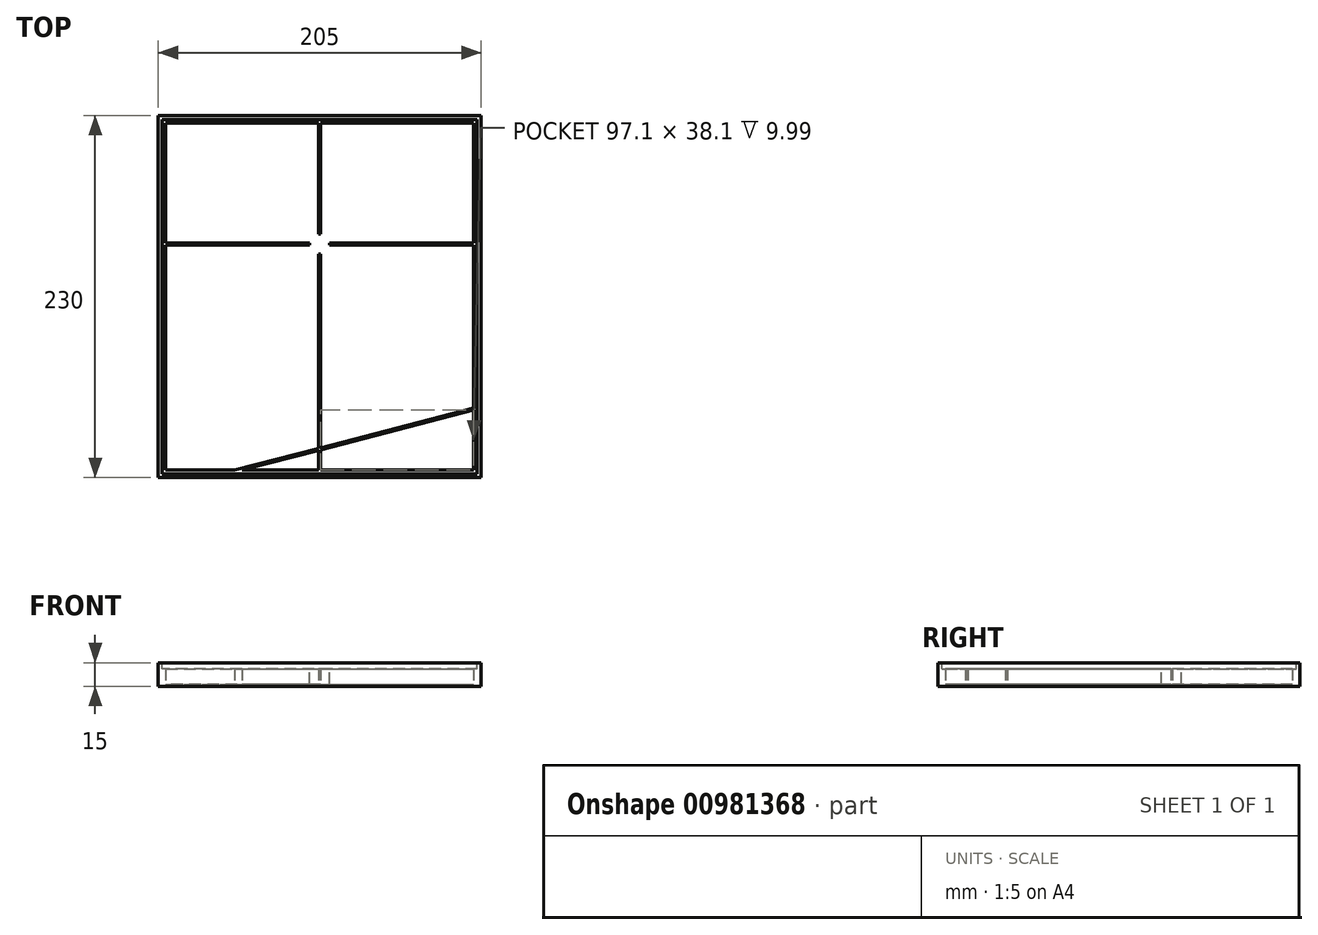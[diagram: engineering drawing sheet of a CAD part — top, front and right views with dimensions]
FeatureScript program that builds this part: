
annotation { "Feature Type Name" : "Feature", "Feature Type Description" : "" }
export const myFeature = defineFeature(function(context is Context, id is Id, definition is map)
    precondition{}
    {
        {
            var Q0;
            Q0=qCreatedBy(makeId("Top.planeOp"),FACE);
            var sketch = newSketch(context, id + "F0", { "sketchPlane" : qUnion([Q0])});
            skLineSegment(sketch, "E0.bottom", {"start": v(0, 0) * mm, "end": v(205, 0) * mm});
            skLineSegment(sketch, "E0.top", {"start": v(0, 230) * mm, "end": v(205, 230) * mm});
            skLineSegment(sketch, "E0.left", {"start": v(0, 0) * mm, "end": v(0, 230) * mm});
            skLineSegment(sketch, "E0.right", {"start": v(205, 0) * mm, "end": v(205, 230) * mm});
            skSolve(sketch);
        }
        {
            var Q0;
            Q0=makeQuery(id+"F0.imprint","IMPRINT",FACE,{"disambiguationData":[TD([[makeQuery(id+"F0.imprint","IMPRINT",EDGE,{"derivedFrom":sQuery(id+"F0.wireOp",EDGE,"E0.bottom")}),1.0]])]});
            extrude(context, id + "F1", {"entities" : qUnion([Q0]), "depth" : 15 * mm, "offsetDistance" : 25 * mm});
        }
        {
            var Q0;
            Q0=makeQuery(id+"F1.opExtrude","CAP_FACE",FACE,{"disambiguationData":[OSD([sQuery(id+"F0.wireOp",EDGE,"E0.bottom"),sQuery(id+"F0.wireOp",EDGE,"E0.top"),sQuery(id+"F0.wireOp",EDGE,"E0.left"),sQuery(id+"F0.wireOp",EDGE,"E0.right")])],"isStart":false});
            var sketch = newSketch(context, id + "F2", { "sketchPlane" : qUnion([Q0])});
            skLineSegment(sketch, "E1.bottom", {"start": v(2.4, 227.6) * mm, "end": v(202.6, 227.6) * mm});
            skLineSegment(sketch, "E1.top", {"start": v(2.4, 2.4) * mm, "end": v(202.6, 2.4) * mm});
            skLineSegment(sketch, "E1.left", {"start": v(2.4, 227.6) * mm, "end": v(2.4, 2.4) * mm});
            skLineSegment(sketch, "E1.right", {"start": v(202.6, 227.6) * mm, "end": v(202.6, 2.4) * mm});
            skSolve(sketch);
        }
        {
            var Q0;
            Q0=makeQuery(id+"F2.imprint","IMPRINT",FACE,{"disambiguationData":[TD([[makeQuery(id+"F2.imprint","IMPRINT",EDGE,{"derivedFrom":sQuery(id+"F2.wireOp",EDGE,"E1.bottom")}),-1.0]])]});
            extrude(context, id + "F3", {"entities" : qUnion([Q0]), "operationType" : NewBodyOperationType.REMOVE, "endBound" : BoundingType.UP_TO_NEXT, "oppositeDirection" : true, "depth" : 25 * mm, "hasOffset" : true, "offsetDistance" : 1.2 * mm});
        }
        {
            var Q0;
            Q0=makeQuery(id+"F3.boolean.opBoolean","COPY",FACE,{"derivedFrom":makeQuery(id+"F3.opExtrude","CAP_FACE",FACE,{"disambiguationData":[OSD([sQuery(id+"F2.wireOp",EDGE,"E1.bottom"),sQuery(id+"F2.wireOp",EDGE,"E1.top"),sQuery(id+"F2.wireOp",EDGE,"E1.left"),sQuery(id+"F2.wireOp",EDGE,"E1.right")])],"isStart":false})});
            var sketch = newSketch(context, id + "F4", { "sketchPlane" : qUnion([Q0])});
            skLineSegment(sketch, "E2.bottom", {"start": v(4.8, 225.2) * mm, "end": v(200.2, 225.2) * mm});
            skLineSegment(sketch, "E2.top", {"start": v(4.8, 4.8) * mm, "end": v(200.2, 4.8) * mm});
            skLineSegment(sketch, "E2.left", {"start": v(4.8, 225.2) * mm, "end": v(4.8, 4.8) * mm});
            skLineSegment(sketch, "E2.right", {"start": v(200.2, 225.2) * mm, "end": v(200.2, 4.8) * mm});
            skLineSegment(sketch, "E3", {"start": v(101.9, 225.2) * mm, "end": v(101.9, 149) * mm});
            skLineSegment(sketch, "E4", {"start": v(101.9, 149) * mm, "end": v(4.8, 149) * mm});
            skLineSegment(sketch, "E5", {"start": v(4.8, 149) * mm, "end": v(4.8, 147.8) * mm});
            skLineSegment(sketch, "E6", {"start": v(4.8, 147.8) * mm, "end": v(101.9, 147.8) * mm});
            skLineSegment(sketch, "E7", {"start": v(101.9, 147.8) * mm, "end": v(101.9, 4.8) * mm});
            skLineSegment(sketch, "E8", {"start": v(101.9, 4.8) * mm, "end": v(103.1, 4.8) * mm});
            skLineSegment(sketch, "E9", {"start": v(103.1, 4.8) * mm, "end": v(103.1, 147.8) * mm});
            skLineSegment(sketch, "E10", {"start": v(103.1, 147.8) * mm, "end": v(200.2, 147.8) * mm});
            skLineSegment(sketch, "E11", {"start": v(200.2, 147.8) * mm, "end": v(200.2, 149) * mm});
            skLineSegment(sketch, "E12", {"start": v(200.2, 149) * mm, "end": v(103.1, 149) * mm});
            skLineSegment(sketch, "E13", {"start": v(103.1, 149) * mm, "end": v(103.1, 225.2) * mm});
            skLineSegment(sketch, "E14", {"start": v(103.1, 225.2) * mm, "end": v(101.9, 225.2) * mm});
            skSolve(sketch);
        }
        {
            var Q0;
            Q0=makeQuery(id+"F4.imprint","IMPRINT",FACE,{"disambiguationData":[TD([[makeQuery(id+"F4.imprint","IMPRINT",EDGE,{"derivedFrom":sQuery(id+"F4.wireOp",EDGE,"E2.bottom")}),1.0]])]});
            var Q1;
            Q1=makeQuery(id+"F4.imprint","IMPRINT",FACE,{"disambiguationData":[TD([[makeQuery(id+"F4.imprint","IMPRINT",EDGE,{"derivedFrom":sQuery(id+"F4.wireOp",EDGE,"E3")}),1.0]])]});
            var Q2;
            Q2=makeQuery(id+"F1.opExtrude","CAP_FACE",FACE,{"disambiguationData":[OSD([sQuery(id+"F0.wireOp",EDGE,"E0.bottom"),sQuery(id+"F0.wireOp",EDGE,"E0.top"),sQuery(id+"F0.wireOp",EDGE,"E0.left"),sQuery(id+"F0.wireOp",EDGE,"E0.right")])],"isStart":false});
            extrude(context, id + "F5", {"entities" : qUnion([Q0, Q1]), "operationType" : NewBodyOperationType.ADD, "endBound" : BoundingType.UP_TO_SURFACE, "depth" : 19.05 * mm, "endBoundEntityFace" : qUnion([Q2]), "hasOffset" : true, "offsetDistance" : 3.8 * mm});
        }
        {
            var Q0;
            Q0=makeQuery(id+"F5.opExtrude","CAP_FACE",FACE,{"disambiguationData":[OSD([sQuery(id+"F2.wireOp",EDGE,"E1.bottom"),sQuery(id+"F2.wireOp",EDGE,"E1.top"),sQuery(id+"F2.wireOp",EDGE,"E1.left"),sQuery(id+"F2.wireOp",EDGE,"E1.right"),sQuery(id+"F4.wireOp",EDGE,"E2.bottom"),sQuery(id+"F4.wireOp",EDGE,"E2.top"),sQuery(id+"F4.wireOp",EDGE,"E2.left"),sQuery(id+"F4.wireOp",EDGE,"E2.right"),sQuery(id+"F4.wireOp",EDGE,"E3"),sQuery(id+"F4.wireOp",EDGE,"E4"),sQuery(id+"F4.wireOp",EDGE,"E6"),sQuery(id+"F4.wireOp",EDGE,"E7"),sQuery(id+"F4.wireOp",EDGE,"E9"),sQuery(id+"F4.wireOp",EDGE,"E10"),sQuery(id+"F4.wireOp",EDGE,"E12"),sQuery(id+"F4.wireOp",EDGE,"E13")])],"isStart":false});
            var sketch = newSketch(context, id + "F6", { "sketchPlane" : qUnion([Q0])});
            skLineSegment(sketch, "E15", {"start": v(103.1, 149) * mm, "end": v(101.9, 147.8) * mm});
            skLineSegment(sketch, "E16", {"start": v(101.9, 147.8) * mm, "end": v(101.9, 149) * mm});
            skLineSegment(sketch, "E17", {"start": v(101.9, 149) * mm, "end": v(103.1, 147.8) * mm});
            skCircle(sketch, "E18", {"center": v(102.5, 148.4) * mm, "radius": 6.35 * mm});
            skSolve(sketch);
        }
        {
            var Q0;
            {var subQ0=sQuery(id+"F6.wireOp",EDGE,"E18");var subQ1=makeQuery(id+"F5.opExtrude","CAP_EDGE",EDGE,{"disambiguationData":[OSD([sQuery(id+"F4.wireOp",EDGE,"E13")])],"isStart":false});var subQ2=makeQuery(id+"F6.imprint","INTERSECT",VERTEX,{"derivedFrom":[subQ1,subQ0]});Q0=makeQuery(id+"F6.imprint","IMPRINT",FACE,{"disambiguationData":[TD([[makeQuery(id+"F6.imprint","IMPRINT",EDGE,{"disambiguationData":[TD([[subQ2,1.0]])],"derivedFrom":subQ0}),1.0]])]});}
            var Q1;
            {var subQ3=sQuery(id+"F6.wireOp",EDGE,"E18");var subQ5=makeQuery(id+"F5.opExtrude","CAP_EDGE",EDGE,{"disambiguationData":[OSD([sQuery(id+"F4.wireOp",EDGE,"E13")])],"isStart":false});var subQ6=makeQuery(id+"F6.imprint","INTERSECT",VERTEX,{"derivedFrom":[subQ5,subQ3]});Q1=makeQuery(id+"F6.imprint","IMPRINT",FACE,{"disambiguationData":[TD([[makeQuery(id+"F6.imprint","IMPRINT",EDGE,{"disambiguationData":[TD([[subQ6,-1.0]])],"derivedFrom":subQ3}),1.0]])]});}
            var Q2;
            {var subQ0=sQuery(id+"F6.wireOp",EDGE,"E18");var subQ1=makeQuery(id+"F5.opExtrude","CAP_EDGE",EDGE,{"disambiguationData":[OSD([sQuery(id+"F4.wireOp",EDGE,"E3")])],"isStart":false});var subQ2=makeQuery(id+"F6.imprint","INTERSECT",VERTEX,{"derivedFrom":[subQ1,subQ0]});Q2=makeQuery(id+"F6.imprint","IMPRINT",FACE,{"disambiguationData":[TD([[makeQuery(id+"F6.imprint","IMPRINT",EDGE,{"disambiguationData":[TD([[subQ2,-1.0]])],"derivedFrom":subQ0}),1.0]])]});}
            var Q3;
            {var subQ0=sQuery(id+"F6.wireOp",EDGE,"E16");Q3=makeQuery(id+"F6.imprint","IMPRINT",FACE,{"disambiguationData":[TD([[makeQuery(id+"F6.imprint","IMPRINT",EDGE,{"derivedFrom":subQ0}),1.0]])]});}
            var Q4;
            {var subQ0=sQuery(id+"F6.wireOp",EDGE,"E16");Q4=makeQuery(id+"F6.imprint","IMPRINT",FACE,{"disambiguationData":[TD([[makeQuery(id+"F6.imprint","IMPRINT",EDGE,{"derivedFrom":subQ0}),-1.0]])]});}
            var Q5;
            {var subQ3=sQuery(id+"F6.wireOp",EDGE,"E18");var subQ5=makeQuery(id+"F5.opExtrude","CAP_EDGE",EDGE,{"disambiguationData":[OSD([sQuery(id+"F4.wireOp",EDGE,"E12")])],"isStart":false});var subQ6=makeQuery(id+"F6.imprint","INTERSECT",VERTEX,{"derivedFrom":[subQ5,subQ3]});Q5=makeQuery(id+"F6.imprint","IMPRINT",FACE,{"disambiguationData":[TD([[makeQuery(id+"F6.imprint","IMPRINT",EDGE,{"disambiguationData":[TD([[subQ6,1.0]])],"derivedFrom":subQ3}),1.0]])]});}
            var Q6;
            {var subQ1=makeQuery(id+"F5.opExtrude","CAP_EDGE",EDGE,{"disambiguationData":[OSD([sQuery(id+"F4.wireOp",EDGE,"E7")])],"isStart":false});var subQ3=sQuery(id+"F6.wireOp",EDGE,"E18");var subQ4=makeQuery(id+"F6.imprint","INTERSECT",VERTEX,{"derivedFrom":[subQ1,subQ3]});Q6=makeQuery(id+"F6.imprint","IMPRINT",FACE,{"disambiguationData":[TD([[makeQuery(id+"F6.imprint","IMPRINT",EDGE,{"disambiguationData":[TD([[subQ4,-1.0]])],"derivedFrom":subQ3}),1.0]])]});}
            var Q7;
            {var subQ0=sQuery(id+"F6.wireOp",EDGE,"E18");var subQ1=makeQuery(id+"F5.opExtrude","CAP_EDGE",EDGE,{"disambiguationData":[OSD([sQuery(id+"F4.wireOp",EDGE,"E9")])],"isStart":false});var subQ2=makeQuery(id+"F6.imprint","INTERSECT",VERTEX,{"derivedFrom":[subQ1,subQ0]});Q7=makeQuery(id+"F6.imprint","IMPRINT",FACE,{"disambiguationData":[TD([[makeQuery(id+"F6.imprint","IMPRINT",EDGE,{"disambiguationData":[TD([[subQ2,-1.0]])],"derivedFrom":subQ0}),1.0]])]});}
            var Q8;
            {var subQ0=sQuery(id+"F6.wireOp",EDGE,"E18");var subQ1=makeQuery(id+"F5.opExtrude","CAP_EDGE",EDGE,{"disambiguationData":[OSD([sQuery(id+"F4.wireOp",EDGE,"E6")])],"isStart":false});var subQ2=makeQuery(id+"F6.imprint","INTERSECT",VERTEX,{"derivedFrom":[subQ1,subQ0]});Q8=makeQuery(id+"F6.imprint","IMPRINT",FACE,{"disambiguationData":[TD([[makeQuery(id+"F6.imprint","IMPRINT",EDGE,{"disambiguationData":[TD([[subQ2,-1.0]])],"derivedFrom":subQ0}),1.0]])]});}
            var Q9;
            {var subQ4=sQuery(id+"F4.wireOp",EDGE,"E12");Q9=makeQuery(id+"F5.boolean.opBoolean","SPLIT",FACE,{"disambiguationData":[TD([makeQuery(id+"F5.opExtrude","SWEPT_FACE",FACE,{"disambiguationData":[OSD([subQ4])]})])],"derivedFrom":makeQuery(id+"F3.boolean.opBoolean","COPY",FACE,{"derivedFrom":makeQuery(id+"F3.opExtrude","CAP_FACE",FACE,{"disambiguationData":[OSD([sQuery(id+"F2.wireOp",EDGE,"E1.bottom"),sQuery(id+"F2.wireOp",EDGE,"E1.top"),sQuery(id+"F2.wireOp",EDGE,"E1.left"),sQuery(id+"F2.wireOp",EDGE,"E1.right")])],"isStart":false})})});}
            extrude(context, id + "F7", {"entities" : qUnion([Q0, Q1, Q2, Q3, Q4, Q5, Q6, Q7, Q8]), "operationType" : NewBodyOperationType.REMOVE, "endBound" : BoundingType.UP_TO_SURFACE, "oppositeDirection" : true, "depth" : 25.4 * mm, "endBoundEntityFace" : qUnion([Q9]), "offsetDistance" : 25.4 * mm});
        }
        {
            var Q0;
            {var subQ3=sQuery(id+"F4.wireOp",EDGE,"E9");var subQ7=makeQuery(id+"F3.boolean.opBoolean","COPY",FACE,{"derivedFrom":makeQuery(id+"F3.opExtrude","CAP_FACE",FACE,{"disambiguationData":[OSD([sQuery(id+"F2.wireOp",EDGE,"E1.bottom"),sQuery(id+"F2.wireOp",EDGE,"E1.top"),sQuery(id+"F2.wireOp",EDGE,"E1.left"),sQuery(id+"F2.wireOp",EDGE,"E1.right")])],"isStart":false})});var subQ11=sQuery(id+"F4.wireOp",EDGE,"E6");var subQ17=sQuery(id+"F4.wireOp",EDGE,"E12");var subQ19=sQuery(id+"F4.wireOp",EDGE,"E3");Q0=makeQuery(id+"F7.boolean.opBoolean","MERGE",FACE,{"derivedFrom":[makeQuery(id+"F5.boolean.opBoolean","SPLIT",FACE,{"disambiguationData":[TD([makeQuery(id+"F5.opExtrude","SWEPT_FACE",FACE,{"disambiguationData":[OSD([subQ19])]})])],"derivedFrom":subQ7}),makeQuery(id+"F5.boolean.opBoolean","SPLIT",FACE,{"disambiguationData":[TD([makeQuery(id+"F5.opExtrude","SWEPT_FACE",FACE,{"disambiguationData":[OSD([subQ17])]})])],"derivedFrom":subQ7}),makeQuery(id+"F5.boolean.opBoolean","SPLIT",FACE,{"disambiguationData":[TD([makeQuery(id+"F5.opExtrude","SWEPT_FACE",FACE,{"disambiguationData":[OSD([subQ11])]})])],"derivedFrom":subQ7}),makeQuery(id+"F5.boolean.opBoolean","SPLIT",FACE,{"disambiguationData":[TD([makeQuery(id+"F5.opExtrude","SWEPT_FACE",FACE,{"disambiguationData":[OSD([subQ3])]})])],"derivedFrom":subQ7})],"fromTools":[makeQuery(id+"F7.opExtrude","CAP_FACE",FACE,{"disambiguationData":[OSD([sQuery(id+"F6.wireOp",EDGE,"E18")])],"isStart":false})]});}
            var sketch = newSketch(context, id + "F8", { "sketchPlane" : qUnion([Q0])});
            skLineSegment(sketch, "E19", {"start": v(48.57, 4.8) * mm, "end": v(200.2, 44.14) * mm});
            skLineSegment(sketch, "E20", {"start": v(200.2, 44.14) * mm, "end": v(200.2, 42.9) * mm});
            skLineSegment(sketch, "E21", {"start": v(200.2, 42.9) * mm, "end": v(53.35, 4.8) * mm});
            skLineSegment(sketch, "E22", {"start": v(53.35, 4.8) * mm, "end": v(48.57, 4.8) * mm});
            skSolve(sketch);
        }
        {
            var Q0;
            {var subQ0=sQuery(id+"F8.wireOp",EDGE,"E20");Q0=makeQuery(id+"F8.imprint","IMPRINT",FACE,{"disambiguationData":[TD([[makeQuery(id+"F8.imprint","IMPRINT",EDGE,{"derivedFrom":subQ0}),-1.0]])]});}
            var Q1;
            {var subQ0=sQuery(id+"F8.wireOp",EDGE,"E22");Q1=makeQuery(id+"F8.imprint","IMPRINT",FACE,{"disambiguationData":[TD([[makeQuery(id+"F8.imprint","IMPRINT",EDGE,{"derivedFrom":subQ0}),1.0]])]});}
            var Q2;
            Q2=makeQuery(id+"F5.opExtrude","CAP_FACE",FACE,{"disambiguationData":[OSD([sQuery(id+"F2.wireOp",EDGE,"E1.bottom"),sQuery(id+"F2.wireOp",EDGE,"E1.top"),sQuery(id+"F2.wireOp",EDGE,"E1.left"),sQuery(id+"F2.wireOp",EDGE,"E1.right"),sQuery(id+"F4.wireOp",EDGE,"E2.bottom"),sQuery(id+"F4.wireOp",EDGE,"E2.top"),sQuery(id+"F4.wireOp",EDGE,"E2.left"),sQuery(id+"F4.wireOp",EDGE,"E2.right"),sQuery(id+"F4.wireOp",EDGE,"E3"),sQuery(id+"F4.wireOp",EDGE,"E4"),sQuery(id+"F4.wireOp",EDGE,"E6"),sQuery(id+"F4.wireOp",EDGE,"E7"),sQuery(id+"F4.wireOp",EDGE,"E9"),sQuery(id+"F4.wireOp",EDGE,"E10"),sQuery(id+"F4.wireOp",EDGE,"E12"),sQuery(id+"F4.wireOp",EDGE,"E13")])],"isStart":false});
            extrude(context, id + "F9", {"entities" : qUnion([Q0, Q1]), "operationType" : NewBodyOperationType.ADD, "endBound" : BoundingType.UP_TO_SURFACE, "depth" : 25.4 * mm, "endBoundEntityFace" : qUnion([Q2]), "offsetDistance" : 25.4 * mm});
        }
    });
